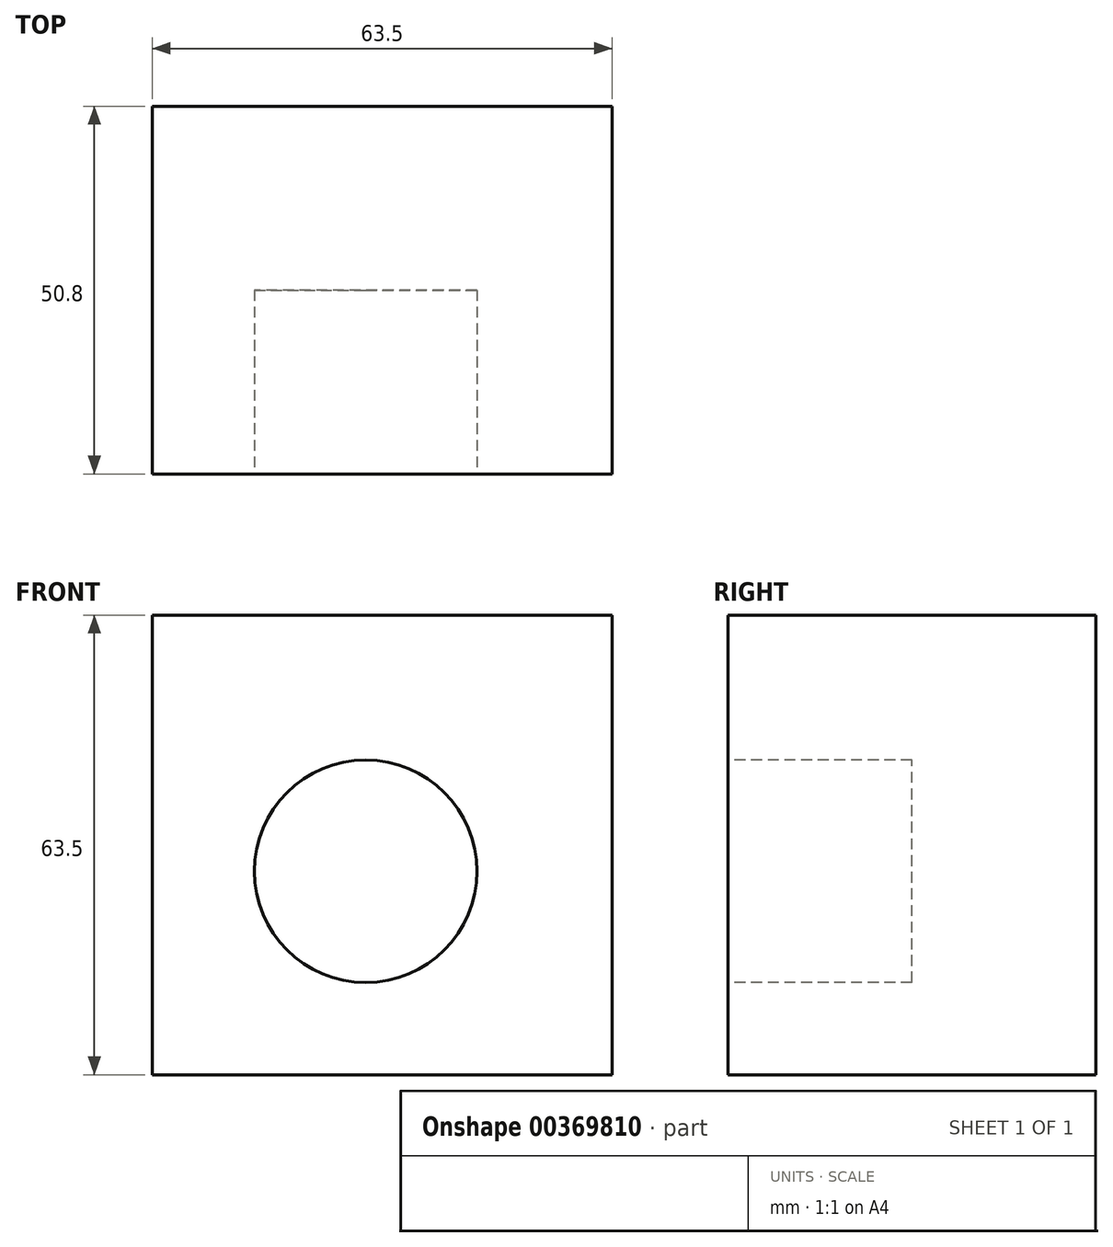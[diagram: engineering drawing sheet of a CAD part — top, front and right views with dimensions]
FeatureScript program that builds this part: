
annotation { "Feature Type Name" : "Feature", "Feature Type Description" : "" }
export const myFeature = defineFeature(function(context is Context, id is Id, definition is map)
    precondition{}
    {
        {
            var Q0;
            Q0=qCreatedBy(makeId("Front.planeOp"),FACE);
            var sketch = newSketch(context, id + "F0", { "sketchPlane" : qUnion([Q0])});
            skLineSegment(sketch, "E0.bottom", {"start": v(0, 0) * mm, "end": v(63.5, 0) * mm});
            skLineSegment(sketch, "E0.top", {"start": v(0, -63.5) * mm, "end": v(63.5, -63.5) * mm});
            skLineSegment(sketch, "E0.left", {"start": v(0, 0) * mm, "end": v(0, -63.5) * mm});
            skLineSegment(sketch, "E0.right", {"start": v(63.5, 0) * mm, "end": v(63.5, -63.5) * mm});
            skSolve(sketch);
        }
        {
            var Q0;
            Q0=makeQuery(id+"F0.imprint","IMPRINT",FACE,{"disambiguationData":[TD([[makeQuery(id+"F0.imprint","IMPRINT",EDGE,{"derivedFrom":sQuery(id+"F0.wireOp",EDGE,"E0.bottom")}),-1.0]])]});
            extrude(context, id + "F1", {"entities" : qUnion([Q0]), "oppositeDirection" : true, "depth" : 50.8 * mm});
        }
        {
            var Q0;
            Q0=makeQuery(id+"F1.opExtrude","CAP_FACE",FACE,{"disambiguationData":[OSD([sQuery(id+"F0.wireOp",EDGE,"E0.bottom"),sQuery(id+"F0.wireOp",EDGE,"E0.top"),sQuery(id+"F0.wireOp",EDGE,"E0.left"),sQuery(id+"F0.wireOp",EDGE,"E0.right")])],"isStart":true});
            var sketch = newSketch(context, id + "F2", { "sketchPlane" : qUnion([Q0])});
            skCircle(sketch, "E1", {"center": v(29.47, -35.4) * mm, "radius": 15.37 * mm});
            skSolve(sketch);
        }
        {
            var Q0;
            Q0 = qSketchRegion(id + "F2", true);
            extrude(context, id + "F3", {"entities" : qUnion([Q0]), "operationType" : NewBodyOperationType.REMOVE, "oppositeDirection" : true, "depth" : 25.4 * mm});
        }
    });
